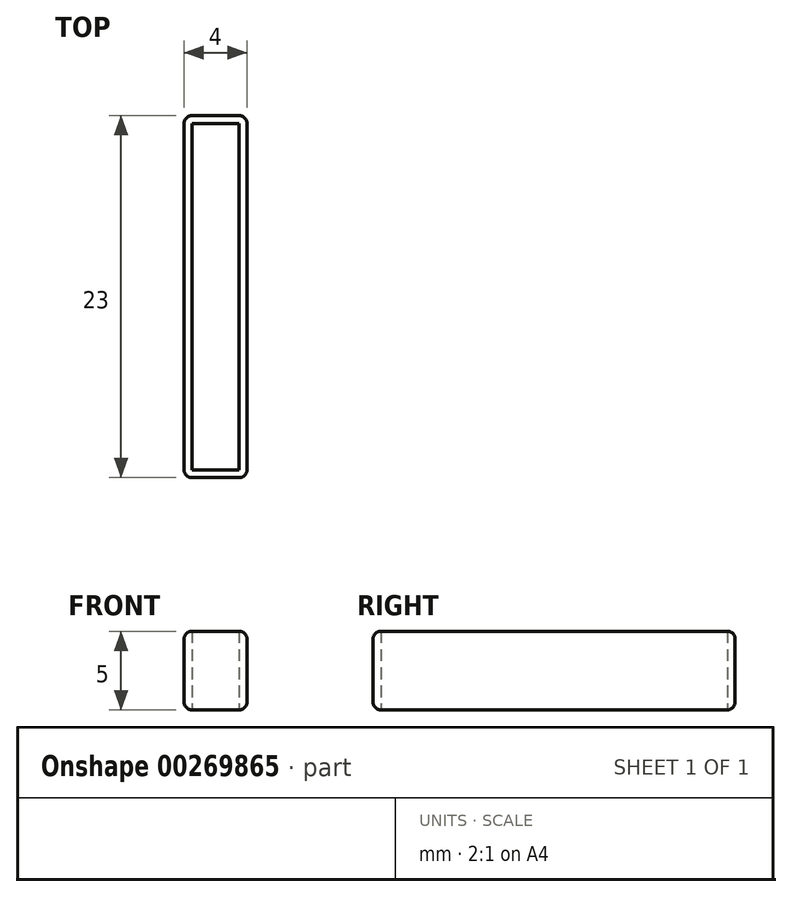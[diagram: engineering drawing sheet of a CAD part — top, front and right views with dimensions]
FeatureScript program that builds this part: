
annotation { "Feature Type Name" : "Feature", "Feature Type Description" : "" }
export const myFeature = defineFeature(function(context is Context, id is Id, definition is map)
    precondition{}
    {
        {
            var Q0;
            Q0=qCreatedBy(makeId("Top.planeOp"),FACE);
            var sketch = newSketch(context, id + "F0", { "sketchPlane" : qUnion([Q0])});
            skLineSegment(sketch, "E0.bottom", {"start": v(0, 0) * mm, "end": v(-3, 0) * mm});
            skLineSegment(sketch, "E0.top", {"start": v(0, 22) * mm, "end": v(-3, 22) * mm});
            skLineSegment(sketch, "E0.left", {"start": v(0, 0) * mm, "end": v(0, 22) * mm});
            skLineSegment(sketch, "E0.right", {"start": v(-3, 0) * mm, "end": v(-3, 22) * mm});
            skLineSegment(sketch, "E1.0", {"start": v(0, 22.5) * mm, "end": v(-3, 22.5) * mm});
            skLineSegment(sketch, "E1.1", {"start": v(0.5, 0) * mm, "end": v(0.5, 22) * mm});
            skLineSegment(sketch, "E1.2", {"start": v(0, -0.5) * mm, "end": v(-3, -0.5) * mm});
            skLineSegment(sketch, "E1.3", {"start": v(-3.5, 0) * mm, "end": v(-3.5, 22) * mm});
            skPoint(sketch, "E2.visualSharp", {"position": v(-3.5, -0.5) * mm});
            skArc(sketch, "E2.filletArc", {"start": v(-3.5, 0) * mm, "mid": v(-3.35, -0.35) * mm, "end": v(-3, -0.5) * mm});
            skPoint(sketch, "E3.visualSharp", {"position": v(0.5, -0.5) * mm});
            skArc(sketch, "E3.filletArc", {"start": v(0, -0.5) * mm, "mid": v(0.35, -0.35) * mm, "end": v(0.5, 0) * mm});
            skPoint(sketch, "E4.visualSharp", {"position": v(-3.5, 22.5) * mm});
            skArc(sketch, "E4.filletArc", {"start": v(-3, 22.5) * mm, "mid": v(-3.35, 22.35) * mm, "end": v(-3.5, 22) * mm});
            skPoint(sketch, "E5.visualSharp", {"position": v(0.5, 22.5) * mm});
            skArc(sketch, "E5.filletArc", {"start": v(0.5, 22) * mm, "mid": v(0.35, 22.35) * mm, "end": v(0, 22.5) * mm});
            skSolve(sketch);
        }
        {
            var Q0;
            Q0 = qSketchRegion(id + "F0", true);
            extrude(context, id + "F1", {"entities" : qUnion([Q0]), "depth" : 5 * mm});
        }
        {
            var Q0;
            Q0=makeQuery(id+"F1.opExtrude","CAP_EDGE",EDGE,{"disambiguationData":[OSD([sQuery(id+"F0.wireOp",EDGE,"E1.3")])],"isStart":true});
            fillet(context, id + "F2", {"entities" : qUnion([Q0]), "radius" : 0.5 * mm, "tangentPropagation" : true, "allowEdgeOverflow" : false});
        }
        {
            var Q0;
            Q0=makeQuery(id+"F1.opExtrude","CAP_EDGE",EDGE,{"disambiguationData":[OSD([sQuery(id+"F0.wireOp",EDGE,"E1.3")])],"isStart":false});
            fillet(context, id + "F3", {"entities" : qUnion([Q0]), "radius" : 0.5 * mm, "tangentPropagation" : true, "allowEdgeOverflow" : false});
        }
    });
